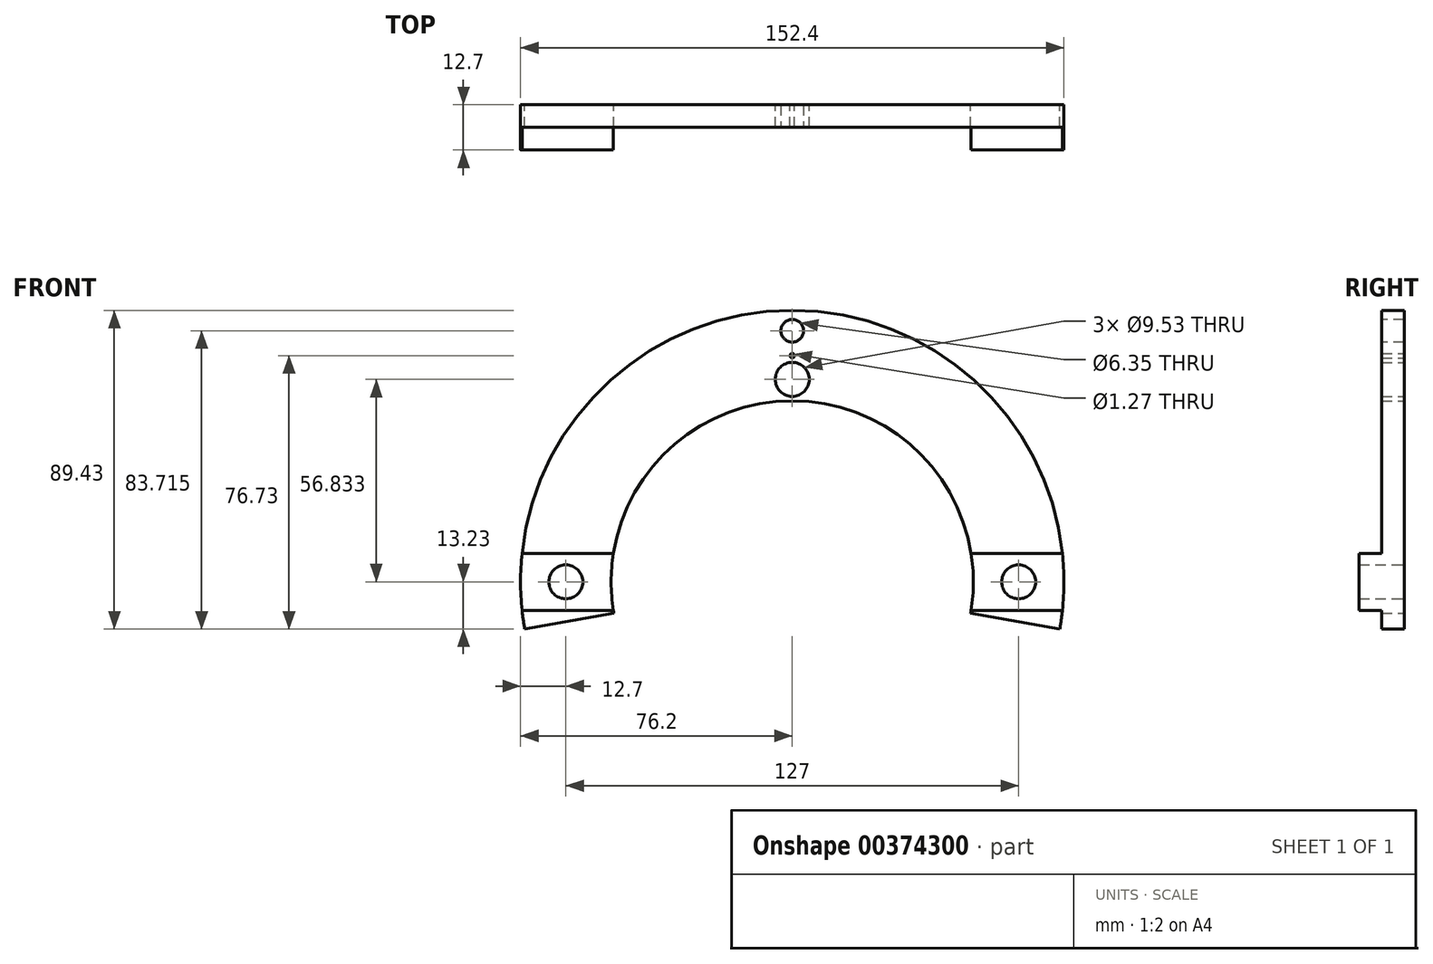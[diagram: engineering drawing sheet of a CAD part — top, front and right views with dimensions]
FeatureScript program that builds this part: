
annotation { "Feature Type Name" : "Feature", "Feature Type Description" : "" }
export const myFeature = defineFeature(function(context is Context, id is Id, definition is map)
    precondition{}
    {
        {
            var Q0;
            Q0=qCreatedBy(makeId("Front.planeOp"),FACE);
            var sketch = newSketch(context, id + "F0", { "sketchPlane" : qUnion([Q0])});
            skArc(sketch, "E0", {"start": v(75.04, -13.23) * mm, "mid": v(0, 76.2) * mm, "end": v(-75.04, -13.23) * mm});
            skCircle(sketch, "E1", {"center": v(-63.5, 0) * mm, "radius": 4.76 * mm});
            skCircle(sketch, "E2", {"center": v(63.5, 0) * mm, "radius": 4.76 * mm});
            skArc(sketch, "E3", {"start": v(62.54, -11.03) * mm, "mid": v(0, 63.5) * mm, "end": v(-62.54, -11.03) * mm, "construction": true});
            skArc(sketch, "E4", {"start": v(50.03, -8.82) * mm, "mid": v(0, 50.8) * mm, "end": v(-50.03, -8.82) * mm});
            skLineSegment(sketch, "E5", {"start": v(-50.03, -8.82) * mm, "end": v(-75.04, -13.23) * mm});
            skLineSegment(sketch, "E6", {"start": v(50.03, -8.82) * mm, "end": v(75.04, -13.23) * mm});
            skCircle(sketch, "E7", {"center": v(0, 56.83) * mm, "radius": 4.76 * mm});
            skSolve(sketch);
        }
        {
            var Q0;
            Q0=makeQuery(id+"F0.imprint","IMPRINT",FACE,{"disambiguationData":[TD([[makeQuery(id+"F0.imprint","IMPRINT",EDGE,{"derivedFrom":sQuery(id+"F0.wireOp",EDGE,"E0")}),1.0]])]});
            extrude(context, id + "F1", {"entities" : qUnion([Q0]), "depth" : 6.35 * mm});
        }
        {
            var Q0;
            Q0=makeQuery(id+"F1.opExtrude","CAP_FACE",FACE,{"disambiguationData":[OSD([sQuery(id+"F0.wireOp",EDGE,"E0"),sQuery(id+"F0.wireOp",EDGE,"E1"),sQuery(id+"F0.wireOp",EDGE,"E2"),sQuery(id+"F0.wireOp",EDGE,"7bfakKx3-WrWB-drmw-14rl-Jtv5k1K2qEE5"),sQuery(id+"F0.wireOp",EDGE,"E4"),sQuery(id+"F0.wireOp",EDGE,"E5"),sQuery(id+"F0.wireOp",EDGE,"E6")])],"isStart":false});
            var sketch = newSketch(context, id + "F2", { "sketchPlane" : qUnion([Q0])});
            skLineSegment(sketch, "E8.bottom", {"start": v(-75.78, 8) * mm, "end": v(-50.17, 8) * mm});
            skLineSegment(sketch, "E8.top", {"start": v(-75.78, -8) * mm, "end": v(-50.17, -8) * mm});
            skArc(sketch, "E9.0", {"start": v(75.78, -8) * mm, "mid": v(76.2, 0) * mm, "end": v(75.78, 8) * mm});
            skArc(sketch, "E10.0", {"start": v(50.17, -8) * mm, "mid": v(50.8, 0) * mm, "end": v(50.17, 8) * mm});
            skLineSegment(sketch, "E11.trimOffspring", {"start": v(50.17, -8) * mm, "end": v(75.78, -8) * mm});
            skLineSegment(sketch, "E12.trimOffspring", {"start": v(50.17, 8) * mm, "end": v(75.78, 8) * mm});
            skArc(sketch, "E13.trimOffspring", {"start": v(-75.78, 8) * mm, "mid": v(-76.2, 0) * mm, "end": v(-75.78, -8) * mm});
            skArc(sketch, "E14.trimOffspring", {"start": v(-50.17, 8) * mm, "mid": v(-50.8, 0) * mm, "end": v(-50.17, -8) * mm});
            skPoint(sketch, "E15.orphan", {"position": v(-75.04, -13.23) * mm});
            skPoint(sketch, "E16.orphan", {"position": v(-50.03, -8.82) * mm});
            skPoint(sketch, "E17.orphan", {"position": v(50.03, -8.82) * mm});
            skPoint(sketch, "E18.orphan", {"position": v(75.04, -13.23) * mm});
            skCircle(sketch, "E19.0", {"center": v(-63.5, 0) * mm, "radius": 4.76 * mm});
            skCircle(sketch, "E20.0", {"center": v(63.5, 0) * mm, "radius": 4.76 * mm});
            skSolve(sketch);
        }
        {
            var Q0;
            Q0=makeQuery(id+"F2.imprint","IMPRINT",FACE,{"disambiguationData":[TD([[makeQuery(id+"F2.imprint","IMPRINT",EDGE,{"derivedFrom":sQuery(id+"F2.wireOp",EDGE,"E8.bottom")}),-1.0]])]});
            var Q1;
            Q1=makeQuery(id+"F2.imprint","IMPRINT",FACE,{"disambiguationData":[TD([[makeQuery(id+"F2.imprint","IMPRINT",EDGE,{"derivedFrom":sQuery(id+"F2.wireOp",EDGE,"E9.0")}),1.0]])]});
            extrude(context, id + "F3", {"entities" : qUnion([Q0, Q1]), "operationType" : NewBodyOperationType.ADD, "depth" : 6.35 * mm});
        }
        {
            var Q0;
            {var subQ0=sQuery(id+"F0.wireOp",EDGE,"E7");var subQ1=sQuery(id+"F0.wireOp",EDGE,"E4");var subQ2=sQuery(id+"F0.wireOp",EDGE,"E0");Q0=makeQuery(id+"F3.boolean.opBoolean","SPLIT",FACE,{"disambiguationData":[TD([makeQuery(id+"F1.opExtrude","SWEPT_FACE",FACE,{"disambiguationData":[OSD([subQ0])]})])],"derivedFrom":makeQuery(id+"F1.opExtrude","CAP_FACE",FACE,{"disambiguationData":[OSD([subQ2,sQuery(id+"F0.wireOp",EDGE,"E1"),sQuery(id+"F0.wireOp",EDGE,"E2"),subQ1,sQuery(id+"F0.wireOp",EDGE,"E5"),sQuery(id+"F0.wireOp",EDGE,"E6"),subQ0])],"isStart":false})});}
            var sketch = newSketch(context, id + "F4", { "sketchPlane" : qUnion([Q0])});
            skCircle(sketch, "E21", {"center": v(0, 70.48) * mm, "radius": 3.18 * mm});
            skCircle(sketch, "E22", {"center": v(0, 0) * mm, "radius": 63.5 * mm, "construction": true});
            skSolve(sketch);
        }
        {
            var Q0;
            Q0=makeQuery(id+"F4.imprint","IMPRINT",FACE,{"disambiguationData":[TD([[makeQuery(id+"F4.imprint","IMPRINT",EDGE,{"derivedFrom":sQuery(id+"F4.wireOp",EDGE,"E21")}),1.0]])]});
            extrude(context, id + "F5", {"entities" : qUnion([Q0]), "operationType" : NewBodyOperationType.REMOVE, "oppositeDirection" : true, "depth" : 6.35 * mm});
        }
        {
            var Q0;
            Q0=makeQuery(id+"F1.opExtrude","CAP_FACE",FACE,{"disambiguationData":[OSD([sQuery(id+"F0.wireOp",EDGE,"E0"),sQuery(id+"F0.wireOp",EDGE,"E1"),sQuery(id+"F0.wireOp",EDGE,"E2"),sQuery(id+"F0.wireOp",EDGE,"E4"),sQuery(id+"F0.wireOp",EDGE,"E5"),sQuery(id+"F0.wireOp",EDGE,"E6"),sQuery(id+"F0.wireOp",EDGE,"E7")])],"isStart":true});
            var sketch = newSketch(context, id + "F6", { "sketchPlane" : qUnion([Q0])});
            skCircle(sketch, "E23", {"center": v(0, 0) * mm, "radius": 63.5 * mm, "construction": true});
            skCircle(sketch, "E24", {"center": v(0, 63.5) * mm, "radius": 0.64 * mm});
            skSolve(sketch);
        }
        {
            var Q0;
            Q0=makeQuery(id+"F6.imprint","IMPRINT",FACE,{"disambiguationData":[TD([[makeQuery(id+"F6.imprint","IMPRINT",EDGE,{"derivedFrom":sQuery(id+"F6.wireOp",EDGE,"E24")}),1.0]])]});
            extrude(context, id + "F7", {"entities" : qUnion([Q0]), "operationType" : NewBodyOperationType.REMOVE, "oppositeDirection" : true, "depth" : 6.35 * mm});
        }
    });
